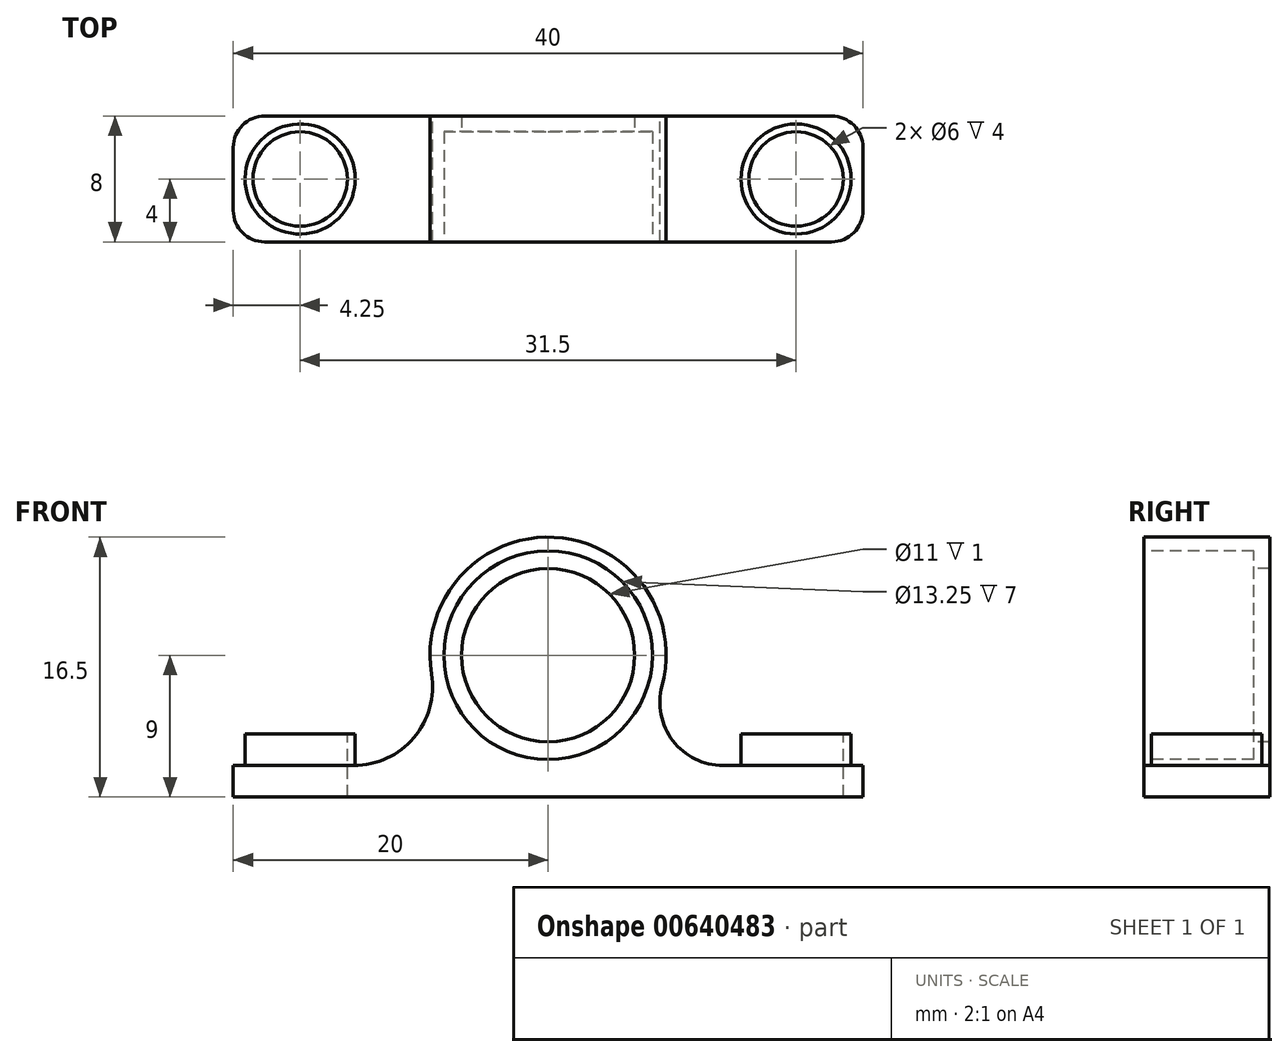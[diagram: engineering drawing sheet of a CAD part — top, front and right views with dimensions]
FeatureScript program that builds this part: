
annotation { "Feature Type Name" : "Feature", "Feature Type Description" : "" }
export const myFeature = defineFeature(function(context is Context, id is Id, definition is map)
    precondition{}
    {
        {
            var Q0;
            Q0=qCreatedBy(makeId("Top.planeOp"),FACE);
            var sketch = newSketch(context, id + "F0", { "sketchPlane" : qUnion([Q0])});
            skLineSegment(sketch, "E0.bottom", {"start": v(-20, 4) * mm, "end": v(20, 4) * mm});
            skLineSegment(sketch, "E0.top", {"start": v(-20, -4) * mm, "end": v(20, -4) * mm});
            skLineSegment(sketch, "E0.left", {"start": v(-20, 4) * mm, "end": v(-20, -4) * mm});
            skLineSegment(sketch, "E0.right", {"start": v(20, 4) * mm, "end": v(20, -4) * mm});
            skSolve(sketch);
        }
        {
            var Q0;
            Q0=makeQuery(id+"F0.imprint","IMPRINT",FACE,{"disambiguationData":[TD([[makeQuery(id+"F0.imprint","IMPRINT",EDGE,{"derivedFrom":sQuery(id+"F0.wireOp",EDGE,"E0.bottom")}),-1.0]])]});
            var sketch = newSketch(context, id + "F1", { "sketchPlane" : qUnion([Q0])});
            skCircle(sketch, "E1", {"center": v(-15.75, 0) * mm, "radius": 3.5 * mm});
            skCircle(sketch, "E2.MirrorC", {"center": v(15.75, 0) * mm, "radius": 3.5 * mm});
            skSolve(sketch);
        }
        {
            var Q0;
            Q0=makeQuery(id+"F0.imprint","IMPRINT",FACE,{"disambiguationData":[TD([[makeQuery(id+"F0.imprint","IMPRINT",EDGE,{"derivedFrom":sQuery(id+"F0.wireOp",EDGE,"E0.bottom")}),-1.0]])]});
            extrude(context, id + "F2", {"entities" : qUnion([Q0]), "endBound" : BoundingType.SYMMETRIC, "depth" : 2 * mm, "offsetDistance" : 25 * mm});
        }
        {
            var Q0;
            Q0 = qSketchRegion(id + "F1", true);
            extrude(context, id + "F3", {"entities" : qUnion([Q0]), "operationType" : NewBodyOperationType.ADD, "depth" : 3 * mm, "offsetDistance" : 25 * mm});
        }
        {
            var Q0;
            Q0=qCreatedBy(makeId("Front.planeOp"),FACE);
            var sketch = newSketch(context, id + "F4", { "sketchPlane" : qUnion([Q0])});
            skCircle(sketch, "E3", {"center": v(0, 8) * mm, "radius": 7.5 * mm});
            skSolve(sketch);
        }
        {
            var Q0;
            Q0=makeQuery(id+"F4.imprint","IMPRINT",FACE,{"disambiguationData":[TD([[makeQuery(id+"F4.imprint","IMPRINT",EDGE,{"derivedFrom":sQuery(id+"F4.wireOp",EDGE,"E3")}),1.0]])]});
            var Q1;
            Q1=sQuery(id+"F4.wireOp",EDGE,"E3");
            extrude(context, id + "F5", {"entities" : qUnion([Q0]), "operationType" : NewBodyOperationType.ADD, "surfaceEntities" : qUnion([Q1]), "endBound" : BoundingType.SYMMETRIC, "depth" : 8 * mm, "offsetDistance" : 25 * mm});
        }
        {
            var Q0;
            Q0=makeQuery(id+"F5.boolean.opBoolean","INTERSECT",EDGE,{"disambiguationData":[OD(1.0)],"derivedFrom":[makeQuery(id+"F2.opExtrude","CAP_FACE",FACE,{"disambiguationData":[OSD([sQuery(id+"F0.wireOp",EDGE,"E0.bottom"),sQuery(id+"F0.wireOp",EDGE,"E0.top"),sQuery(id+"F0.wireOp",EDGE,"E0.left"),sQuery(id+"F0.wireOp",EDGE,"E0.right")])],"isStart":false}),makeQuery(id+"F5.opExtrude","SWEPT_FACE",FACE,{"disambiguationData":[OSD([sQuery(id+"F4.wireOp",EDGE,"E3")])]})]});
            fillet(context, id + "F6", {"entities" : qUnion([Q0]), "radius" : 4 * mm, "tangentPropagation" : true, "allowEdgeOverflow" : false});
        }
        {
            var Q0;
            Q0=makeQuery(id+"F5.boolean.opBoolean","INTERSECT",EDGE,{"disambiguationData":[OD(0.0)],"derivedFrom":[makeQuery(id+"F2.opExtrude","CAP_FACE",FACE,{"disambiguationData":[OSD([sQuery(id+"F0.wireOp",EDGE,"E0.bottom"),sQuery(id+"F0.wireOp",EDGE,"E0.top"),sQuery(id+"F0.wireOp",EDGE,"E0.left"),sQuery(id+"F0.wireOp",EDGE,"E0.right")])],"isStart":false}),makeQuery(id+"F5.opExtrude","SWEPT_FACE",FACE,{"disambiguationData":[OSD([sQuery(id+"F4.wireOp",EDGE,"E3")])]})]});
            fillet(context, id + "F7", {"entities" : qUnion([Q0]), "radius" : 5 * mm, "tangentPropagation" : true, "allowEdgeOverflow" : false});
        }
        {
            var Q0;
            Q0=makeQuery(id+"F5.opExtrude","CAP_FACE",FACE,{"disambiguationData":[OSD([sQuery(id+"F4.wireOp",EDGE,"E3")])],"isStart":false});
            var sketch = newSketch(context, id + "F8", { "sketchPlane" : qUnion([Q0])});
            skPoint(sketch, "E4", {"position": v(0, 8) * mm});
            skSolve(sketch);
        }
        {
            var Q0;
            Q0=sQuery(id+"F8.wireOp",VERTEX,"E4");
            var Q1;
            Q1=makeQuery(id+"F2.opExtrude","SWEPT_BODY",BODY,{"disambiguationData":[OSD([sQuery(id+"F0.wireOp",EDGE,"E0.bottom"),sQuery(id+"F0.wireOp",EDGE,"E0.top"),sQuery(id+"F0.wireOp",EDGE,"E0.left"),sQuery(id+"F0.wireOp",EDGE,"E0.right")])]});
            hole(context, id + "F9", {"style" : HoleStyle.C_BORE, "endStyle" : HoleEndStyle.THROUGH, "holeDiameter" : 11 * mm, "cBoreDiameter" : 13.25 * mm, "cBoreDepth" : 7 * mm, "majorDiameter" : 5 * mm, "isTappedThrough" : true, "tappedDepth" : 12 * mm, "tapClearance" : 3, "startFromSketch" : true, "locations" : qUnion([Q0]), "scope" : qUnion([Q1])});
        }
        {
            var Q0;
            Q0=makeQuery(id+"F3.opExtrude","CAP_FACE",FACE,{"disambiguationData":[OSD([sQuery(id+"F1.wireOp",EDGE,"E2.MirrorC")])],"isStart":false});
            var sketch = newSketch(context, id + "F10", { "sketchPlane" : qUnion([Q0])});
            skPoint(sketch, "E5", {"position": v(15.75, 0) * mm});
            skSolve(sketch);
        }
        {
            var Q0;
            Q0=makeQuery(id+"F3.opExtrude","CAP_FACE",FACE,{"disambiguationData":[OSD([sQuery(id+"F1.wireOp",EDGE,"E1")])],"isStart":false});
            var sketch = newSketch(context, id + "F11", { "sketchPlane" : qUnion([Q0])});
            skPoint(sketch, "E6", {"position": v(-15.75, 0) * mm});
            skSolve(sketch);
        }
        {
            var Q0;
            Q0=sQuery(id+"F10.wireOp",VERTEX,"E5");
            var Q1;
            Q1=sQuery(id+"F11.wireOp",VERTEX,"E6");
            var Q2;
            Q2=makeQuery(id+"F2.opExtrude","SWEPT_BODY",BODY,{"disambiguationData":[OSD([sQuery(id+"F0.wireOp",EDGE,"E0.bottom"),sQuery(id+"F0.wireOp",EDGE,"E0.top"),sQuery(id+"F0.wireOp",EDGE,"E0.left"),sQuery(id+"F0.wireOp",EDGE,"E0.right")])]});
            hole(context, id + "F12", {"style" : HoleStyle.SIMPLE, "endStyle" : HoleEndStyle.THROUGH, "holeDiameter" : 6 * mm, "majorDiameter" : 5 * mm, "isTappedThrough" : true, "tappedDepth" : 12 * mm, "tapClearance" : 3, "startFromSketch" : true, "locations" : qUnion([Q0, Q1]), "scope" : qUnion([Q2])});
        }
        {
            var Q0;
            Q0=makeQuery(id+"F2.opExtrude","SWEPT_EDGE",EDGE,{"disambiguationData":[OSD([sQuery(id+"F0.wireOp",EDGE,"E0.top"),sQuery(id+"F0.wireOp",EDGE,"E0.left")])]});
            var Q1;
            Q1=makeQuery(id+"F2.opExtrude","SWEPT_EDGE",EDGE,{"disambiguationData":[OSD([sQuery(id+"F0.wireOp",EDGE,"E0.bottom"),sQuery(id+"F0.wireOp",EDGE,"E0.left")])]});
            var Q2;
            Q2=makeQuery(id+"F2.opExtrude","SWEPT_EDGE",EDGE,{"disambiguationData":[OSD([sQuery(id+"F0.wireOp",EDGE,"E0.bottom"),sQuery(id+"F0.wireOp",EDGE,"E0.right")])]});
            var Q3;
            Q3=makeQuery(id+"F2.opExtrude","SWEPT_EDGE",EDGE,{"disambiguationData":[OSD([sQuery(id+"F0.wireOp",EDGE,"E0.top"),sQuery(id+"F0.wireOp",EDGE,"E0.right")])]});
            fillet(context, id + "F13", {"entities" : qUnion([Q0, Q1, Q2, Q3]), "radius" : 2 * mm, "tangentPropagation" : true, "allowEdgeOverflow" : false});
        }
    });
